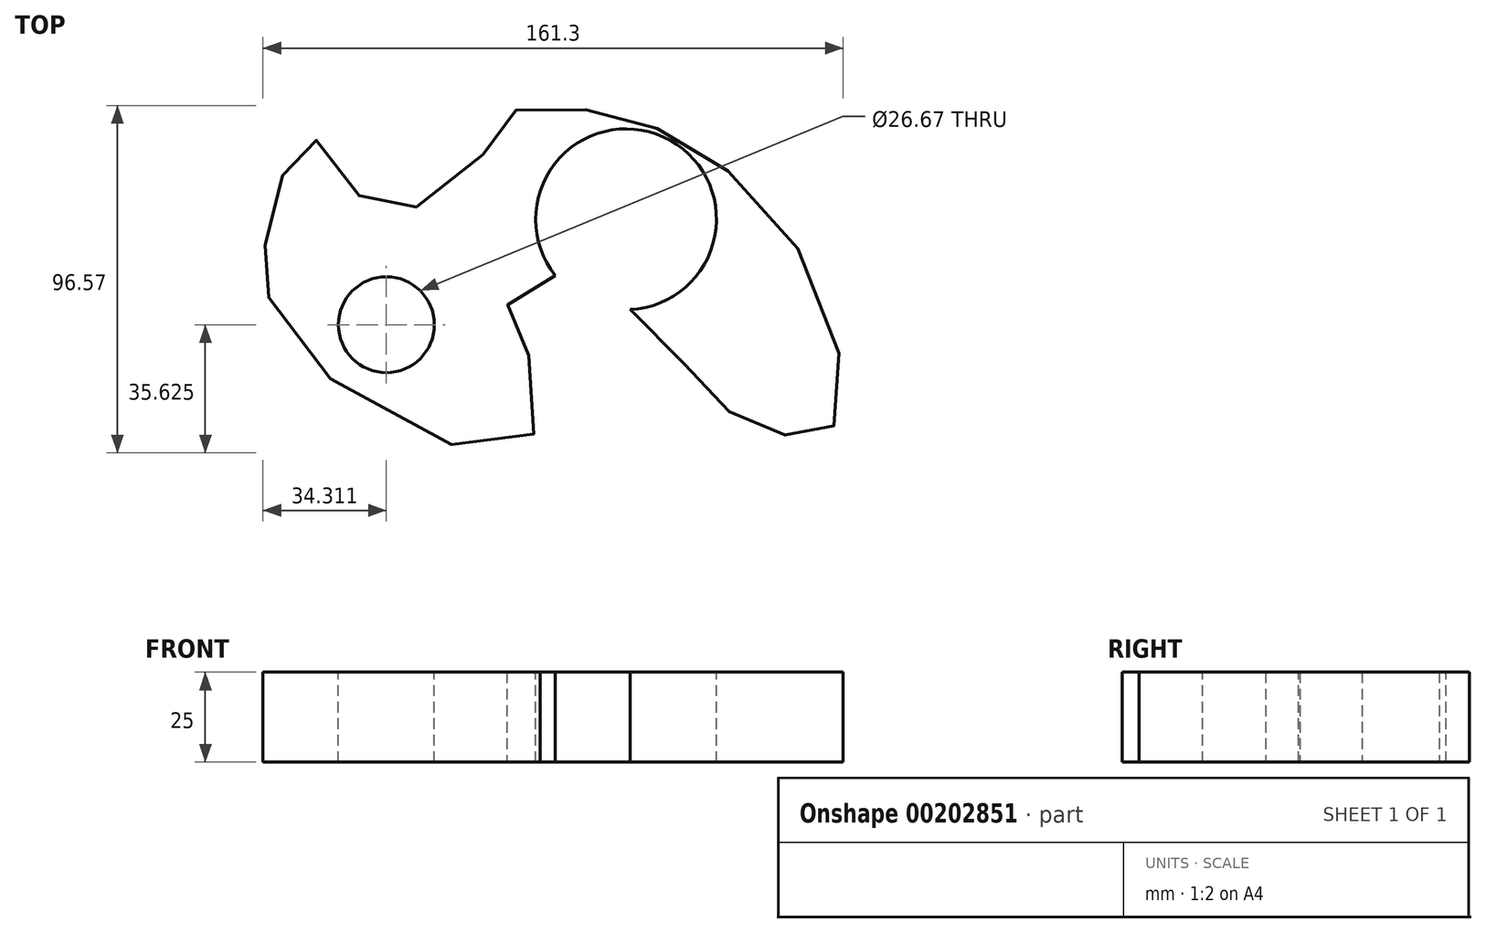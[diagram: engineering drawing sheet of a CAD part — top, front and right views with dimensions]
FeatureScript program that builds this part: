
annotation { "Feature Type Name" : "Feature", "Feature Type Description" : "" }
export const myFeature = defineFeature(function(context is Context, id is Id, definition is map)
    precondition{}
    {
        {
            var Q0;
            Q0=qCreatedBy(makeId("Top.planeOp"),FACE);
            var sketch = newSketch(context, id + "F0", { "sketchPlane" : qUnion([Q0])});
            skFitSpline(sketch, "E0", {"points": [v(-115.97, 9.76) * mm, v(-117.83, 0) * mm, v(-106.48, -25.9) * mm, v(-46.16, -51.79) * mm, v(-43.6, -26.8) * mm, v(-50.02, -12.88) * mm, v(-39.15, -4) * mm, v(-13.4, -15.24) * mm, v(3.94, -33.96) * mm, v(18.33, -45.89) * mm, v(34.44, -48.34) * mm, v(42.48, -43.05) * mm, v(32.97, 0) * mm, v(0, 32.94) * mm, v(-23.89, 41.38) * mm, v(-47.74, 41.97) * mm, v(-55.93, 30.71) * mm, v(-81.24, 13.49) * mm, v(-95.27, 23.67) * mm, v(-106.58, 34.77) * mm, v(-115.97, 9.76) * mm]});
            skSolve(sketch);
        }
        {
            var Q0;
            Q0 = qSketchRegion(id + "F0", true);
            var Q1;
            Q1=makeQuery(id+"F0.imprint","IMPRINT",FACE,{"disambiguationData":[TD([[makeQuery(id+"F0.imprint","IMPRINT",EDGE,{"derivedFrom":sQuery(id+"F0.wireOp",EDGE,"E0")}),1.0]])]});
            extrude(context, id + "F1", {"entities" : qUnion([Q0, Q1]), "depth" : 25 * mm});
        }
        {
            var Q0;
            Q0=makeQuery(id+"F1.opExtrude","CAP_FACE",FACE,{"disambiguationData":[OSD([sQuery(id+"F0.wireOp",EDGE,"E0")])],"isStart":false});
            var sketch = newSketch(context, id + "F2", { "sketchPlane" : qUnion([Q0])});
            skCircle(sketch, "E1", {"center": v(-83.53, -17.6) * mm, "radius": 13.34 * mm});
            skCircle(sketch, "E2", {"center": v(-16.9, 11.74) * mm, "radius": 25.12 * mm});
            skSolve(sketch);
        }
        {
            var Q0;
            Q0 = qSketchRegion(id + "F2", true);
            extrude(context, id + "F3", {"entities" : qUnion([Q0]), "operationType" : NewBodyOperationType.REMOVE, "endBound" : BoundingType.THROUGH_ALL, "oppositeDirection" : true, "depth" : 25 * mm});
        }
    });
